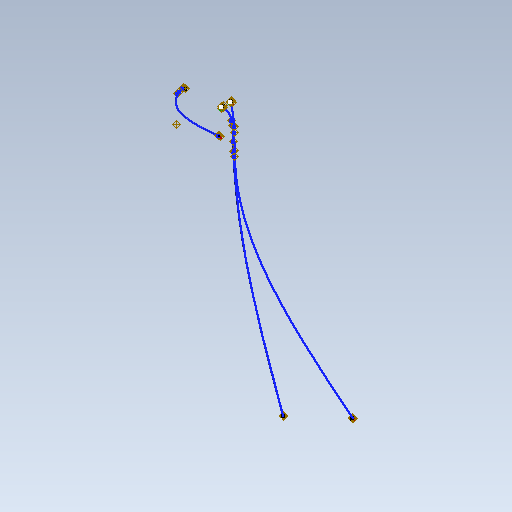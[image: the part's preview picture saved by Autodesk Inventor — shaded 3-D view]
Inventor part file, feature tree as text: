
AUTODESK INVENTOR PART (.ipt)
format: ipt  version: 2020 (Build 240168000, 168)  size: 236,032 bytes
history: native  units: mm (DEFAULTED — no unit token found)
features: other x64, plane x3, sketch x3
bodies: Body1 (feature_tree), Body2 (feature_tree), Body3 (feature_tree)
feature tree (70):
  other  "Origen"
  other  "Punto de trabajo25"
  other  "Punto de trabajo127"
  other  "Punto de trabajo128"
  other  "Cable1:1"
  other  "Punto de trabajo129"
  other  "Punto de trabajo130"
  other  "Cable1:2"
  other  "Punto de trabajo131"
  other  "Punto de trabajo132"
  other  "Cable2:1"
  other  "Punto de trabajo133"
  other  "Punto de trabajo134"
  other  "Cable2:2"
  other  "Punto de trabajo135"
  other  "Punto de trabajo136"
  other  "Cable2:3"
  other  "Punto de trabajo137"
  other  "Punto de trabajo138"
  other  "Cable2:4"
  other  "Punto de trabajo139"
  other  "Punto de trabajo140"
  other  "Cable3:1"
  other  "Punto de trabajo141"
  other  "Punto de trabajo142"
  other  "Cable3:2"
  other  "Punto de trabajo143"
  other  "Punto de trabajo144"
  other  "Cable3:3"
  other  "Punto de trabajo145"
  other  "Punto de trabajo146"
  other  "Cable3:4"
  other  "Punto de trabajo147"
  other  "Punto de trabajo148"
  other  "Segmento2"
  other  "Punto de trabajo149"
  other  "Punto de trabajo150"
  other  "Punto de trabajo151"
  other  "Punto de trabajo152"
  plane  "Plano de trabajo6"
  other  "Punto de trabajo153"
  other  "Punto de trabajo154"
  other  "Segmento3"
  other  "Punto de trabajo155"
  other  "Punto de trabajo156"
  other  "Punto de trabajo157"
  other  "Punto de trabajo158"
  plane  "Plano de trabajo7"
  other  "Punto de trabajo159"
  other  "Punto de trabajo160"
  other  "Segmento1"
  other  "Punto de trabajo161"
  other  "Punto de trabajo162"
  other  "Punto de trabajo163"
  plane  "Plano de trabajo8"
  other  "Plano YZ"
  other  "Plano XZ"
  other  "Plano XY"
  other  "Eje X"
  other  "Eje Y"
  other  "Eje Z"
  sketch  "Boceto6"  dims[d2=0.0mm d3=0.0mm]
  other  "Sup2"
  sketch  "Boceto7"  dims[d4=0.0mm d5=0.0mm]
  other  "Sup3"
  sketch  "Boceto8"  dims[d6=0.0mm d7=0.0mm]
  other  "Sup4"
  other  "SuperficieBarrido2"
  other  "SuperficieBarrido3"
  other  "SuperficieBarrido4"
